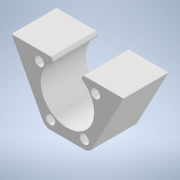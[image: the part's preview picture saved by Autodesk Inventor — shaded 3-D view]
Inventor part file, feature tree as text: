
AUTODESK INVENTOR PART (.ipt)
format: ipt  version: 2020 (Build 240168000, 168)  size: 143,360 bytes
history: native  units: in
note: dims shown in document units (in); Inventor stores cm internally (conversion verified against a paired STEP export)
features: other x4, reference x2, extrude x1, sketch x1
ambient origin geometry x8: Origin, YZ Plane, XZ Plane, XY Plane, X Axis, Y Axis, Z Axis, Center Point
bodies: Solid1 (feature_tree)
feature tree (8):
  extrude  "Extrusion1"  Depth=0.0625in
  sketch  "Sketch1"  dims[d0=0.2in d1=0.2677in d2=0.3961in d6=1.0in d7=0.0in d8=0.0625in]
  reference  "Reference1"
  reference  "Reference2"
  other  "<userpath>\Documents\FRC\2020\IntakeShooter\spacers.iam"
  other  "spacers.iam"
  other  "VersaFrame_Side_Bearing_Gusset_217-3553:2"
  other  "1x1x18:1"
